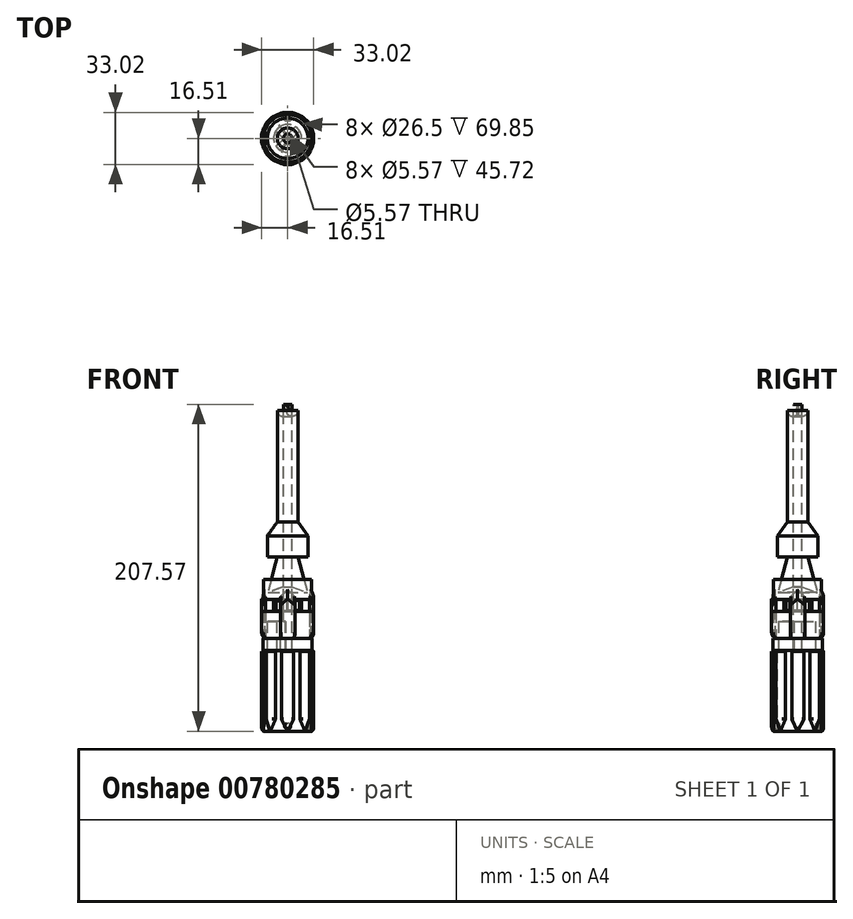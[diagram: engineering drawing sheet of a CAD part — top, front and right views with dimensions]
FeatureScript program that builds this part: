
annotation { "Feature Type Name" : "Feature", "Feature Type Description" : "" }
export const myFeature = defineFeature(function(context is Context, id is Id, definition is map)
    precondition{}
    {
        {
            var Q0;
            Q0=qCreatedBy(makeId("Right.planeOp"),FACE);
            var sketch = newSketch(context, id + "F0", { "sketchPlane" : qUnion([Q0])});
            skLineSegment(sketch, "E0", {"start": v(0, 0) * mm, "end": v(0, 228.6) * mm});
            skLineSegment(sketch, "E1", {"start": v(0, 0) * mm, "end": v(-15.24, 0) * mm});
            skLineSegment(sketch, "E2", {"start": v(-15.24, 0) * mm, "end": v(-15.24, 51.26) * mm});
            skLineSegment(sketch, "E3", {"start": v(-15.24, 76.2) * mm, "end": v(-8.9, 76.2) * mm});
            skLineSegment(sketch, "E4", {"start": v(-8.9, 76.2) * mm, "end": v(-8.9, 83.82) * mm});
            skLineSegment(sketch, "E5", {"start": v(-8.9, 83.82) * mm, "end": v(-15.24, 83.82) * mm});
            skLineSegment(sketch, "E6", {"start": v(-15.24, 83.82) * mm, "end": v(-15.24, 96.52) * mm});
            skLineSegment(sketch, "E7", {"start": v(-15.24, 96.52) * mm, "end": v(-8.9, 96.52) * mm});
            skLineSegment(sketch, "E8", {"start": v(-8.9, 96.52) * mm, "end": v(0, 96.52) * mm});
            skLineSegment(sketch, "E9", {"start": v(-15.24, 51.26) * mm, "end": v(-15.62, 51.26) * mm});
            skLineSegment(sketch, "E10", {"start": v(-15.62, 51.26) * mm, "end": v(-15.62, 58.88) * mm});
            skLineSegment(sketch, "E11", {"start": v(-15.62, 58.88) * mm, "end": v(-15.24, 58.88) * mm});
            skLineSegment(sketch, "E12.trimOffspring", {"start": v(-15.24, 58.88) * mm, "end": v(-15.24, 76.2) * mm});
            skSolve(sketch);
        }
        {
            var Q0;
            {var subQ0=sQuery(id+"F0.wireOp",EDGE,"E1");Q0=makeQuery(id+"F0.imprint","IMPRINT",FACE,{"disambiguationData":[TD([[makeQuery(id+"F0.imprint","IMPRINT",EDGE,{"derivedFrom":subQ0}),-1.0]])]});}
            var Q1;
            Q1=sQuery(id+"F0.wireOp",EDGE,"E0");
            revolve(context, id + "F1", {"surfaceOperationType" : NewSurfaceOperationType.NEW, "entities" : qUnion([Q0]), "axis" : qUnion([Q1]), "revolveType" : RevolveType.FULL});
        }
        {
            var Q0;
            Q0=qCreatedBy(makeId("Front.planeOp"),FACE);
            cPlane(context, id + "F2", {"entities" : qUnion([Q0]), "cplaneType" : CPlaneType.OFFSET, "offset" : 15.24 * mm, "oppositeDirection" : true, "width" : 152.4 * mm, "height" : 152.4 * mm});
        }
        {
            var Q0;
            Q0=qCreatedBy(id+"F2.planeOp",FACE);
            var sketch = newSketch(context, id + "F3", { "sketchPlane" : qUnion([Q0])});
            skLineSegment(sketch, "E13.top", {"start": v(0, 50.8) * mm, "end": v(-3.81, 50.8) * mm});
            skLineSegment(sketch, "E13.right", {"start": v(-3.81, 7.62) * mm, "end": v(-3.81, 50.8) * mm});
            skLineSegment(sketch, "E14.top", {"start": v(0, 50.8) * mm, "end": v(3.8, 50.8) * mm});
            skLineSegment(sketch, "E14.right", {"start": v(3.81, 7.62) * mm, "end": v(3.8, 50.8) * mm});
            skLineSegment(sketch, "E15", {"start": v(3.81, 7.62) * mm, "end": v(0, 0) * mm});
            skLineSegment(sketch, "E16", {"start": v(-3.81, 7.62) * mm, "end": v(0, 0) * mm});
            skSolve(sketch);
        }
        {
            var Q0;
            Q0=makeQuery(id+"F3.imprint","IMPRINT",FACE,{"disambiguationData":[TD([[makeQuery(id+"F3.imprint","IMPRINT",EDGE,{"derivedFrom":sQuery(id+"F3.wireOp",EDGE,"E13.top")}),1.0]])]});
            extrude(context, id + "F4", {"entities" : qUnion([Q0]), "operationType" : NewBodyOperationType.ADD, "oppositeDirection" : true, "depth" : 1.27 * mm, "offsetDistance" : 25.4 * mm, "hasSecondDirection" : true, "secondDirectionOppositeDirection" : false, "secondDirectionDepth" : 6.35 * mm});
        }
        {
            var Q0;
            Q0=makeQuery(id+"F4.opExtrude","CAP_EDGE",EDGE,{"disambiguationData":[OSD([sQuery(id+"F3.wireOp",EDGE,"E13.right")])],"isStart":false});
            var Q1;
            Q1=makeQuery(id+"F4.opExtrude","CAP_EDGE",EDGE,{"disambiguationData":[OSD([sQuery(id+"F3.wireOp",EDGE,"E14.right")])],"isStart":false});
            var Q2;
            Q2=makeQuery(id+"F4.opExtrude","CAP_EDGE",EDGE,{"disambiguationData":[OSD([sQuery(id+"F3.wireOp",EDGE,"E16")])],"isStart":false});
            var Q3;
            Q3=makeQuery(id+"F4.opExtrude","CAP_EDGE",EDGE,{"disambiguationData":[OSD([sQuery(id+"F3.wireOp",EDGE,"E15")])],"isStart":false});
            fillet(context, id + "F5", {"entities" : qUnion([Q0, Q1, Q2, Q3]), "radius" : 1.27 * mm, "tangentPropagation" : true, "allowEdgeOverflow" : false});
        }
        {
            var Q0;
            Q0=qCreatedBy(makeId("Front.planeOp"),FACE);
            var sketch = newSketch(context, id + "F6", { "sketchPlane" : qUnion([Q0])});
            skLineSegment(sketch, "E17", {"start": v(0, 0) * mm, "end": v(0, 228.6) * mm});
            skSolve(sketch);
        }
        {
            var Q0;
            Q0=makeQuery(id+"F1.opRevolve","SWEPT_BODY",BODY,{"disambiguationData":[OSD([sQuery(id+"F0.wireOp",EDGE,"E0"),sQuery(id+"F0.wireOp",EDGE,"E1"),sQuery(id+"F0.wireOp",EDGE,"E2"),sQuery(id+"F0.wireOp",EDGE,"E3"),sQuery(id+"F0.wireOp",EDGE,"E4"),sQuery(id+"F0.wireOp",EDGE,"E5"),sQuery(id+"F0.wireOp",EDGE,"E6"),sQuery(id+"F0.wireOp",EDGE,"E7"),sQuery(id+"F0.wireOp",EDGE,"E8")])]});
            var Q1;
            Q1=sQuery(id+"F6.wireOp",EDGE,"E17");
            circularPattern(context, id + "F7", {"entities" : qUnion([Q0]), "axis" : qUnion([Q1]), "angle" : 360 * degree, "instanceCount" : 8, "equalSpace" : true});
        }
        {
            var Q0;
            Q0=makeQuery(id+"F1.opRevolve","SWEPT_FACE",FACE,{"disambiguationData":[OSD([sQuery(id+"F0.wireOp",EDGE,"E11")])]});
            var sketch = newSketch(context, id + "F8", { "sketchPlane" : qUnion([Q0])});
            skArc(sketch, "E18", {"start": v(15.83, -4.7) * mm, "mid": v(16.5, -0.03) * mm, "end": v(15.85, 4.63) * mm});
            skArc(sketch, "E19.0", {"start": v(13.93, -4.38) * mm, "mid": v(14.6, -0.02) * mm, "end": v(13.94, 4.35) * mm});
            skLineSegment(sketch, "E20", {"start": v(13.93, -4.38) * mm, "end": v(15.83, -4.7) * mm});
            skLineSegment(sketch, "E21", {"start": v(13.94, 4.35) * mm, "end": v(15.85, 4.63) * mm});
            skPoint(sketch, "E22.start.orphan", {"position": v(14.6, 0) * mm});
            skSolve(sketch);
        }
        {
            var Q0;
            Q0 = qSketchRegion(id + "F8", true);
            extrude(context, id + "F9", {"entities" : qUnion([Q0]), "depth" : 31.75 * mm, "offsetDistance" : 25.4 * mm});
        }
        {
            var Q0;
            Q0=makeQuery(id+"F9.opExtrude","CAP_EDGE",EDGE,{"disambiguationData":[OSD([sQuery(id+"F8.wireOp",EDGE,"E21")])],"isStart":false});
            var Q1;
            Q1=makeQuery(id+"F9.opExtrude","CAP_EDGE",EDGE,{"disambiguationData":[OSD([sQuery(id+"F8.wireOp",EDGE,"E20")])],"isStart":false});
            chamfer(context, id + "F10", {"entities" : qUnion([Q0, Q1]), "width" : 5.08 * mm, "tangentPropagation" : true});
        }
        {
            var Q0;
            Q0=makeQuery(id+"F10.opChamfer","BLEND_EDGE",EDGE,{"blendedFrom":[makeQuery(id+"F9.opExtrude","CAP_EDGE",EDGE,{"disambiguationData":[OSD([sQuery(id+"F8.wireOp",EDGE,"E20")])],"isStart":false}),makeQuery(id+"F9.opExtrude","SWEPT_FACE",FACE,{"disambiguationData":[OSD([sQuery(id+"F8.wireOp",EDGE,"E18")])]})],"blendedInto":[makeQuery(id+"F9.opExtrude","SWEPT_FACE",FACE,{"disambiguationData":[OSD([sQuery(id+"F8.wireOp",EDGE,"E18")])]})]});
            var Q1;
            Q1=makeQuery(id+"F10.opChamfer","BLEND_EDGE",EDGE,{"blendedFrom":[makeQuery(id+"F9.opExtrude","CAP_EDGE",EDGE,{"disambiguationData":[OSD([sQuery(id+"F8.wireOp",EDGE,"E21")])],"isStart":false}),makeQuery(id+"F9.opExtrude","SWEPT_FACE",FACE,{"disambiguationData":[OSD([sQuery(id+"F8.wireOp",EDGE,"E18")])]})],"blendedInto":[makeQuery(id+"F9.opExtrude","SWEPT_FACE",FACE,{"disambiguationData":[OSD([sQuery(id+"F8.wireOp",EDGE,"E18")])]})]});
            fillet(context, id + "F11", {"entities" : qUnion([Q0, Q1]), "radius" : 5.08 * mm, "tangentPropagation" : true, "allowEdgeOverflow" : false});
        }
        {
            var Q0;
            Q0=makeQuery(id+"F9.opExtrude","CAP_EDGE",EDGE,{"disambiguationData":[OSD([sQuery(id+"F8.wireOp",EDGE,"E18")])],"isStart":true});
            fillet(context, id + "F12", {"entities" : qUnion([Q0]), "radius" : 5.08 * mm, "tangentPropagation" : true, "allowEdgeOverflow" : false});
        }
        {
            var Q0;
            Q0=makeQuery(id+"F12.opFillet","BLEND_EDGE",EDGE,{"blendedFrom":[makeQuery(id+"F9.opExtrude","CAP_EDGE",EDGE,{"disambiguationData":[OSD([sQuery(id+"F8.wireOp",EDGE,"E18")])],"isStart":true}),makeQuery(id+"F9.opExtrude","SWEPT_FACE",FACE,{"disambiguationData":[OSD([sQuery(id+"F8.wireOp",EDGE,"E20")])]})],"blendedInto":[makeQuery(id+"F9.opExtrude","SWEPT_FACE",FACE,{"disambiguationData":[OSD([sQuery(id+"F8.wireOp",EDGE,"E20")])]})]});
            var Q1;
            Q1=makeQuery(id+"F12.opFillet","BLEND_EDGE",EDGE,{"blendedFrom":[makeQuery(id+"F9.opExtrude","CAP_EDGE",EDGE,{"disambiguationData":[OSD([sQuery(id+"F8.wireOp",EDGE,"E18")])],"isStart":true}),makeQuery(id+"F9.opExtrude","SWEPT_FACE",FACE,{"disambiguationData":[OSD([sQuery(id+"F8.wireOp",EDGE,"E21")])]})],"blendedInto":[makeQuery(id+"F9.opExtrude","SWEPT_FACE",FACE,{"disambiguationData":[OSD([sQuery(id+"F8.wireOp",EDGE,"E21")])]})]});
            fillet(context, id + "F13", {"entities" : qUnion([Q0, Q1]), "radius" : 0.38 * mm, "tangentPropagation" : true, "allowEdgeOverflow" : false});
        }
        {
            var Q0;
            Q0=makeQuery(id+"F9.opExtrude","SWEPT_BODY",BODY,{"disambiguationData":[OSD([sQuery(id+"F8.wireOp",EDGE,"E18"),sQuery(id+"F8.wireOp",EDGE,"E19.0"),sQuery(id+"F8.wireOp",EDGE,"E20"),sQuery(id+"F8.wireOp",EDGE,"E21")])]});
            var Q1;
            Q1=sQuery(id+"F6.wireOp",EDGE,"E17");
            circularPattern(context, id + "F14", {"entities" : qUnion([Q0]), "axis" : qUnion([Q1]), "angle" : 360 * degree, "instanceCount" : 4, "equalSpace" : true});
        }
        {
            var Q0;
            Q0=qCreatedBy(makeId("Front.planeOp"),FACE);
            var sketch = newSketch(context, id + "F15", { "sketchPlane" : qUnion([Q0])});
            skLineSegment(sketch, "E23", {"start": v(0, 92.64) * mm, "end": v(0, 207.57) * mm});
            skLineSegment(sketch, "E24", {"start": v(0, 207.57) * mm, "end": v(6.6, 207.57) * mm});
            skLineSegment(sketch, "E25", {"start": v(6.6, 207.57) * mm, "end": v(6.6, 132.9) * mm});
            skLineSegment(sketch, "E26", {"start": v(6.6, 132.9) * mm, "end": v(12.94, 124.1) * mm});
            skLineSegment(sketch, "E27", {"start": v(12.94, 124.1) * mm, "end": v(12.94, 110.74) * mm});
            skLineSegment(sketch, "E28", {"start": v(12.94, 110.74) * mm, "end": v(6.6, 110.74) * mm});
            skLineSegment(sketch, "E29", {"start": v(6.6, 110.74) * mm, "end": v(12.55, 88.13) * mm});
            skLineSegment(sketch, "E30", {"start": v(12.55, 88.13) * mm, "end": v(0, 92.64) * mm});
            skSolve(sketch);
        }
        {
            var Q0;
            Q0 = qSketchRegion(id + "F15", true);
            var Q1;
            Q1=sQuery(id+"F6.wireOp",EDGE,"E17");
            revolve(context, id + "F16", {"surfaceOperationType" : NewSurfaceOperationType.NEW, "entities" : qUnion([Q0]), "axis" : qUnion([Q1]), "revolveType" : RevolveType.FULL});
        }
        {
            var Q0;
            Q0=makeQuery(id+"F16.opRevolve","SWEPT_EDGE",EDGE,{"disambiguationData":[OSD([sQuery(id+"F15.wireOp",EDGE,"E24"),sQuery(id+"F15.wireOp",EDGE,"E25")])]});
            fillet(context, id + "F17", {"entities" : qUnion([Q0]), "radius" : 3.8 * mm, "tangentPropagation" : true, "allowEdgeOverflow" : false});
        }
        {
            var Q0;
            Q0=qCreatedBy(makeId("Right.planeOp"),FACE);
            var Q1;
            Q1=sQuery(id+"F6.wireOp",EDGE,"E17");
            cPlane(context, id + "F18", {"entities" : qUnion([Q0, Q1]), "cplaneType" : CPlaneType.LINE_ANGLE, "offset" : 25.4 * mm, "angle" : 45 * degree, "width" : 152.4 * mm, "height" : 152.4 * mm});
        }
        {
            var Q0;
            Q0=qCreatedBy(id+"F18.planeOp",FACE);
            var sketch = newSketch(context, id + "F19", { "sketchPlane" : qUnion([Q0])});
            skLineSegment(sketch, "E31.bottom", {"start": v(2.07, 82.73) * mm, "end": v(-1.74, 82.73) * mm});
            skLineSegment(sketch, "E31.top", {"start": v(2.07, 76.38) * mm, "end": v(-1.74, 76.38) * mm});
            skLineSegment(sketch, "E31.left", {"start": v(2.07, 82.73) * mm, "end": v(2.07, 76.38) * mm});
            skLineSegment(sketch, "E31.right", {"start": v(-1.74, 82.73) * mm, "end": v(-1.74, 76.38) * mm});
            skSolve(sketch);
        }
        {
            var Q0;
            Q0 = qSketchRegion(id + "F19", true);
            extrude(context, id + "F20", {"entities" : qUnion([Q0]), "operationType" : NewBodyOperationType.REMOVE, "depth" : 8.9 * mm, "offsetDistance" : 25.4 * mm, "hasSecondDirection" : true, "secondDirectionOppositeDirection" : true, "secondDirectionDepth" : 8.9 * mm});
        }
        {
            var Q0;
            Q0=qCreatedBy(makeId("Front.planeOp"),FACE);
            var Q1;
            Q1=sQuery(id+"F6.wireOp",EDGE,"E17");
            cPlane(context, id + "F21", {"entities" : qUnion([Q0, Q1]), "cplaneType" : CPlaneType.LINE_ANGLE, "offset" : 25.4 * mm, "angle" : 225 * degree, "width" : 152.4 * mm, "height" : 152.4 * mm});
        }
        {
            var Q0;
            Q0=qCreatedBy(id+"F21.planeOp",FACE);
            var sketch = newSketch(context, id + "F22", { "sketchPlane" : qUnion([Q0])});
            skLineSegment(sketch, "E32.bottom", {"start": v(-2.08, 82.92) * mm, "end": v(1.73, 82.92) * mm});
            skLineSegment(sketch, "E32.top", {"start": v(-2.08, 76.57) * mm, "end": v(1.73, 76.57) * mm});
            skLineSegment(sketch, "E32.left", {"start": v(-2.08, 82.92) * mm, "end": v(-2.08, 76.57) * mm});
            skLineSegment(sketch, "E32.right", {"start": v(1.73, 82.92) * mm, "end": v(1.73, 76.57) * mm});
            skSolve(sketch);
        }
        {
            var Q0;
            Q0 = qSketchRegion(id + "F22", true);
            extrude(context, id + "F23", {"entities" : qUnion([Q0]), "operationType" : NewBodyOperationType.REMOVE, "oppositeDirection" : true, "depth" : 25.4 * mm, "offsetDistance" : 25.4 * mm, "hasSecondDirection" : true, "secondDirectionOppositeDirection" : false, "secondDirectionDepth" : 25.4 * mm});
        }
        {
            var Q0;
            Q0=makeQuery(id+"F1.opRevolve","SWEPT_FACE",FACE,{"disambiguationData":[OSD([sQuery(id+"F0.wireOp",EDGE,"E1")])]});
            var sketch = newSketch(context, id + "F24", { "sketchPlane" : qUnion([Q0])});
            skCircle(sketch, "E33", {"center": v(0, 0) * mm, "radius": 15.16 * mm});
            skCircle(sketch, "E34.0", {"center": v(0, 0) * mm, "radius": 13.25 * mm});
            skSolve(sketch);
        }
        {
            var Q0;
            Q0=makeQuery(id+"F24.imprint","IMPRINT",FACE,{"disambiguationData":[TD([[makeQuery(id+"F24.imprint","IMPRINT",EDGE,{"derivedFrom":sQuery(id+"F24.wireOp",EDGE,"E34.0")}),1.0]])]});
            extrude(context, id + "F25", {"entities" : qUnion([Q0]), "operationType" : NewBodyOperationType.REMOVE, "oppositeDirection" : true, "depth" : 50.8 * mm, "offsetDistance" : 25.4 * mm});
        }
        {
            var Q0;
            Q0=makeQuery(id+"F16.opRevolve","SWEPT_FACE",FACE,{"disambiguationData":[OSD([sQuery(id+"F15.wireOp",EDGE,"E24")])]});
            extrude(context, id + "F26", {"entities" : qUnion([Q0]), "operationType" : NewBodyOperationType.REMOVE, "oppositeDirection" : true, "depth" : 190.5 * mm, "offsetDistance" : 25.4 * mm});
        }
        {
            var Q0;
            Q0=makeQuery(id+"F25.boolean.opBoolean","COPY",FACE,{"disambiguationData":[OD(0.0)],"derivedFrom":makeQuery(id+"F25.opExtrude","CAP_FACE",FACE,{"disambiguationData":[OSD([sQuery(id+"F24.wireOp",EDGE,"E34.0")])],"isStart":false})});
            var sketch = newSketch(context, id + "F27", { "sketchPlane" : qUnion([Q0])});
            skLineSegment(sketch, "E35", {"start": v(-1.46, -2.37) * mm, "end": v(-7.12, -11.18) * mm});
            skLineSegment(sketch, "E36", {"start": v(1.57, 2.3) * mm, "end": v(7.24, 11.1) * mm});
            skLineSegment(sketch, "E37", {"start": v(7.24, 11.1) * mm, "end": v(1.57, 2.3) * mm});
            skLineSegment(sketch, "E38", {"start": v(1.46, -2.37) * mm, "end": v(3.3, -12.84) * mm});
            skLineSegment(sketch, "E39", {"start": v(-1.57, 2.3) * mm, "end": v(-4.84, 12.34) * mm});
            skSolve(sketch);
        }
        {
            var Q0;
            {var subQ0=sQuery(id+"F27.wireOp",EDGE,"E35");Q0=makeQuery(id+"F27.imprint","IMPRINT",FACE,{"disambiguationData":[TD([[makeQuery(id+"F27.imprint","IMPRINT",EDGE,{"derivedFrom":subQ0}),-1.0]])]});}
            var Q1;
            {var subQ0=sQuery(id+"F27.wireOp",EDGE,"E37");Q1=makeQuery(id+"F27.imprint","IMPRINT",FACE,{"disambiguationData":[TD([[makeQuery(id+"F27.imprint","IMPRINT",EDGE,{"derivedFrom":subQ0}),1.0]])]});}
            extrude(context, id + "F28", {"entities" : qUnion([Q0, Q1]), "operationType" : NewBodyOperationType.REMOVE, "oppositeDirection" : true, "depth" : 19.05 * mm, "offsetDistance" : 25.4 * mm});
        }
        {
            var Q0;
            Q0=qCreatedBy(id+"F2.planeOp",FACE);
            var sketch = newSketch(context, id + "F29", { "sketchPlane" : qUnion([Q0])});
            skCircle(sketch, "E40", {"center": v(0, 3.18) * mm, "radius": 1.9 * mm});
            skLineSegment(sketch, "E41", {"start": v(0, 1.27) * mm, "end": v(0, 0) * mm});
            skSolve(sketch);
        }
        {
            var Q0;
            Q0 = qSketchRegion(id + "F29", true);
            extrude(context, id + "F30", {"entities" : qUnion([Q0]), "depth" : 3.8 * mm, "offsetDistance" : 25.4 * mm});
        }
        {
            var Q0;
            Q0=makeQuery(id+"F30.opExtrude","SWEPT_BODY",BODY,{"disambiguationData":[OSD([sQuery(id+"F29.wireOp",EDGE,"E40")])]});
            var Q1;
            Q1=qCreatedBy(makeId("Front.planeOp"),FACE);
            mirror(context, id + "F31", {"entities" : qUnion([Q0]), "mirrorPlane" : qUnion([Q1])});
        }
        {
            var Q0;
            Q0=makeQuery(id+"F30.opExtrude","CAP_EDGE",EDGE,{"disambiguationData":[OSD([sQuery(id+"F29.wireOp",EDGE,"E40")])],"isStart":false});
            var Q1;
            Q1=makeQuery(id+"F31.opPattern","COPY",EDGE,{"derivedFrom":makeQuery(id+"F30.opExtrude","CAP_EDGE",EDGE,{"disambiguationData":[OSD([sQuery(id+"F29.wireOp",EDGE,"E40")])],"isStart":false}),"instanceName":"1"});
            fillet(context, id + "F32", {"entities" : qUnion([Q0, Q1]), "radius" : 0.13 * mm, "tangentPropagation" : true, "allowEdgeOverflow" : false});
        }
    });
